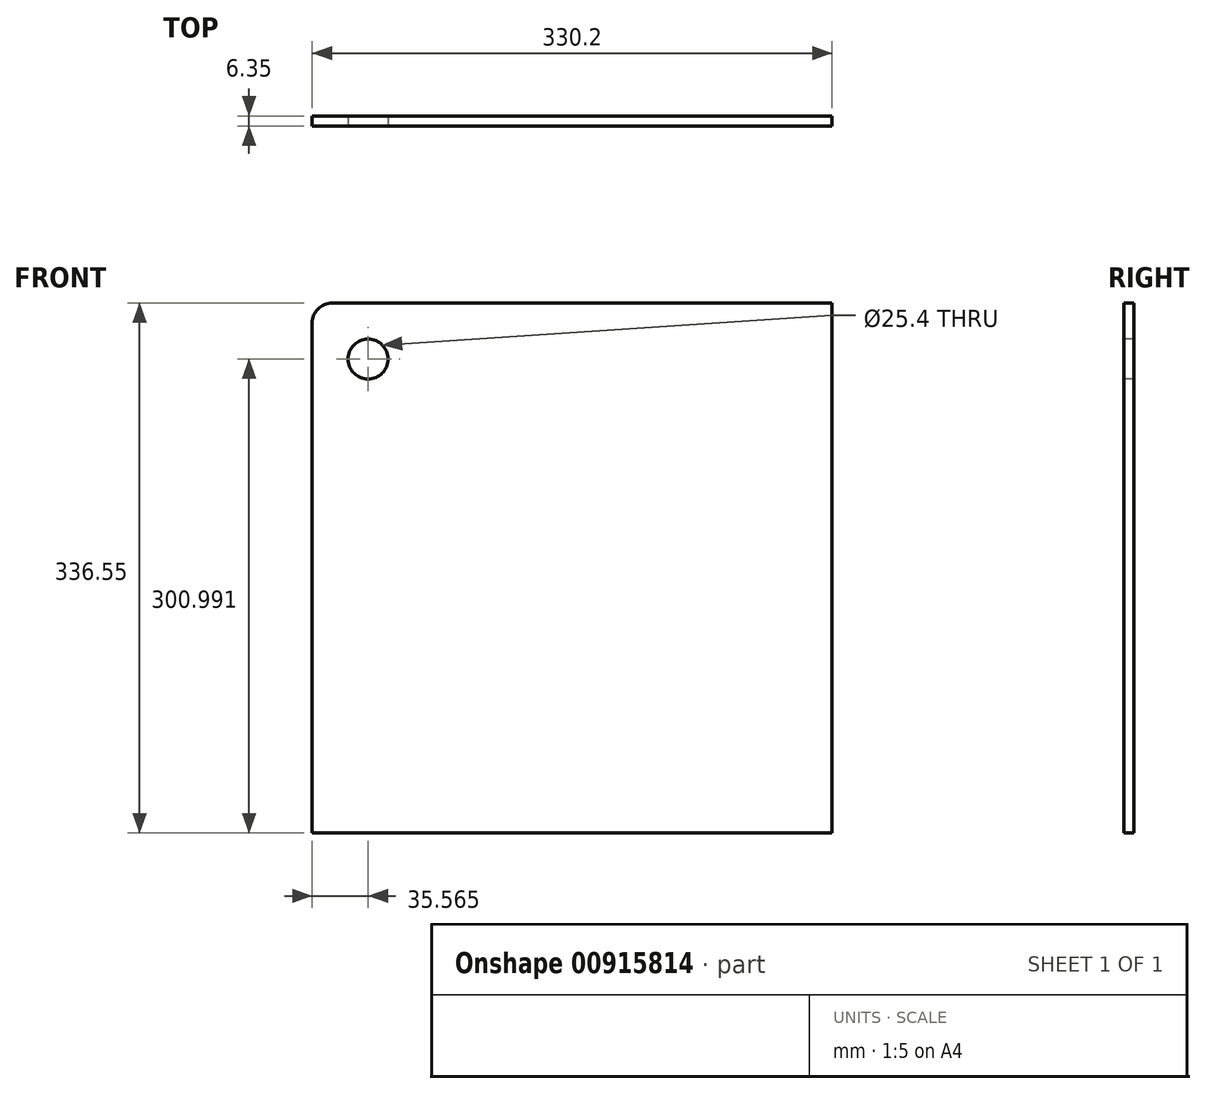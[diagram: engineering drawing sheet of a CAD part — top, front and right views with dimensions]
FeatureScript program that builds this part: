
annotation { "Feature Type Name" : "Feature", "Feature Type Description" : "" }
export const myFeature = defineFeature(function(context is Context, id is Id, definition is map)
    precondition{}
    {
        {
            var Q0;
            Q0=qCreatedBy(makeId("Front.planeOp"),FACE);
            var sketch = newSketch(context, id + "F0", { "sketchPlane" : qUnion([Q0])});
            skLineSegment(sketch, "E0.bottom", {"start": v(-179.9, 197.47) * mm, "end": v(150.3, 197.47) * mm});
            skLineSegment(sketch, "E0.top", {"start": v(-179.9, -139.08) * mm, "end": v(150.3, -139.08) * mm});
            skLineSegment(sketch, "E0.left", {"start": v(-179.9, 197.47) * mm, "end": v(-179.9, -139.08) * mm});
            skLineSegment(sketch, "E0.right", {"start": v(150.3, 197.47) * mm, "end": v(150.3, -139.08) * mm});
            skSolve(sketch);
        }
        {
            var Q0;
            Q0 = qSketchRegion(id + "F0", true);
            extrude(context, id + "F1", {"entities" : qUnion([Q0]), "oppositeDirection" : true, "depth" : 6.35 * mm, "offsetDistance" : 25.4 * mm});
        }
        {
            var Q0;
            Q0=makeQuery(id+"F1.opExtrude","SWEPT_EDGE",EDGE,{"disambiguationData":[OSD([sQuery(id+"F0.wireOp",EDGE,"E0.bottom"),sQuery(id+"F0.wireOp",EDGE,"E0.left")])]});
            fillet(context, id + "F2", {"entities" : qUnion([Q0]), "radius" : 12.7 * mm, "tangentPropagation" : true, "allowEdgeOverflow" : false});
        }
        {
            var Q0;
            Q0=makeQuery(id+"F1.opExtrude","CAP_FACE",FACE,{"disambiguationData":[OSD([sQuery(id+"F0.wireOp",EDGE,"E0.bottom"),sQuery(id+"F0.wireOp",EDGE,"E0.top"),sQuery(id+"F0.wireOp",EDGE,"E0.left"),sQuery(id+"F0.wireOp",EDGE,"E0.right")])],"isStart":true});
            var sketch = newSketch(context, id + "F3", { "sketchPlane" : qUnion([Q0])});
            skCircle(sketch, "E1", {"center": v(-144.34, 161.91) * mm, "radius": 12.7 * mm});
            skSolve(sketch);
        }
        {
            var Q0;
            Q0 = qSketchRegion(id + "F3", true);
            extrude(context, id + "F4", {"entities" : qUnion([Q0]), "operationType" : NewBodyOperationType.REMOVE, "oppositeDirection" : true, "depth" : 25.4 * mm, "offsetDistance" : 25.4 * mm});
        }
    });
